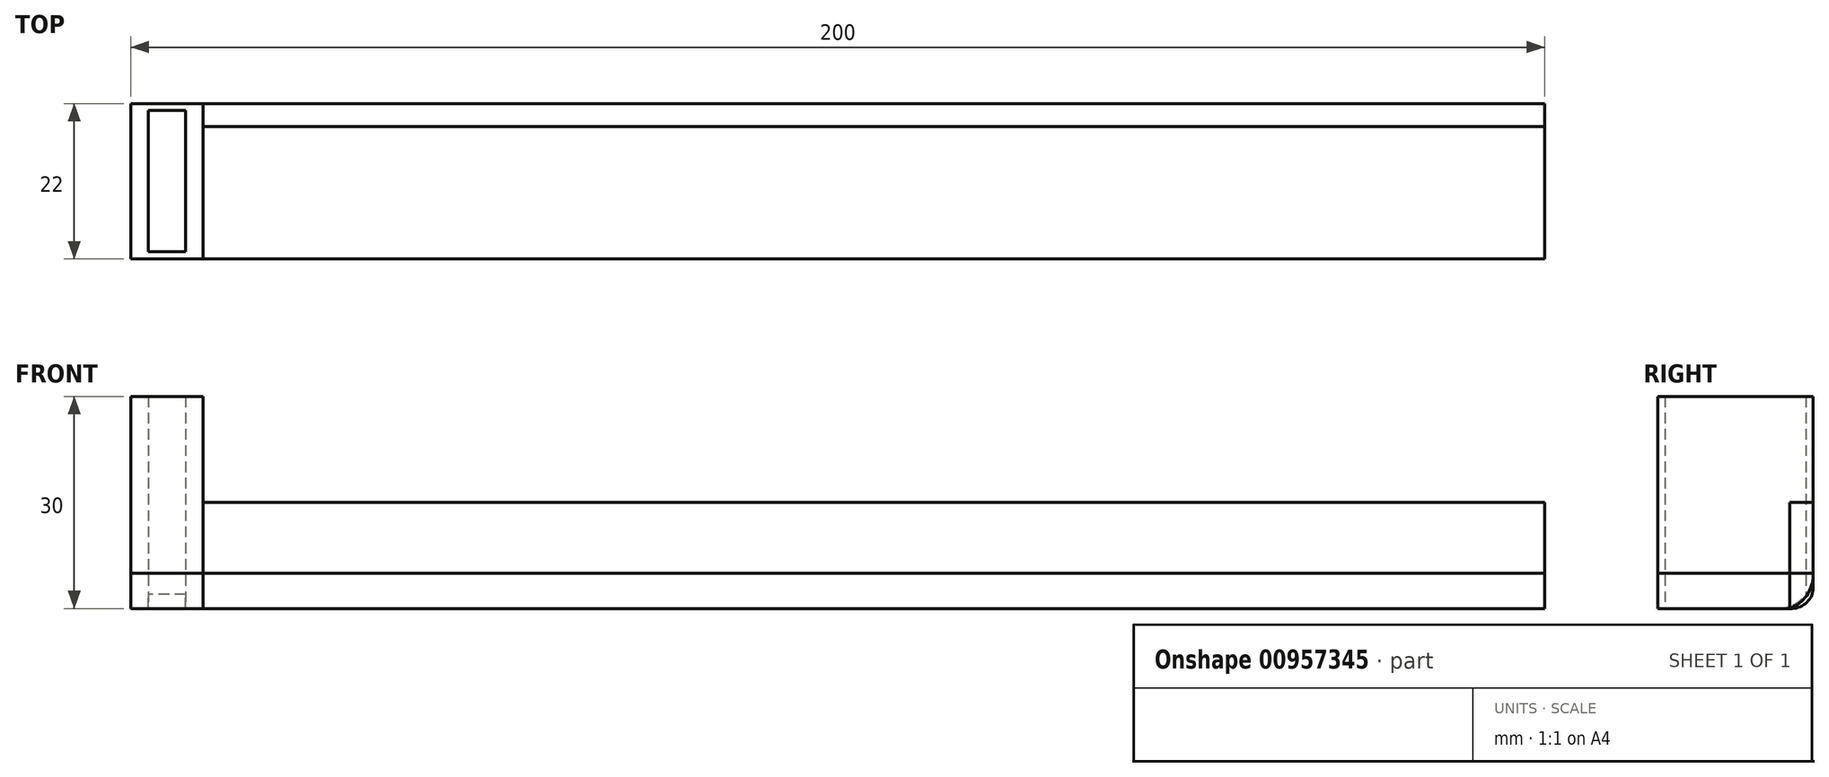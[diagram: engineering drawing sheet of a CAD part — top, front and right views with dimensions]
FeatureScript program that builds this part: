
annotation { "Feature Type Name" : "Feature", "Feature Type Description" : "" }
export const myFeature = defineFeature(function(context is Context, id is Id, definition is map)
    precondition{}
    {
        {
            var Q0;
            Q0=qCreatedBy(makeId("Top.planeOp"),FACE);
            var sketch = newSketch(context, id + "F0", { "sketchPlane" : qUnion([Q0])});
            skLineSegment(sketch, "E0.bottom", {"start": v(-42.3, 31.22) * mm, "end": v(157.7, 31.22) * mm});
            skLineSegment(sketch, "E0.top", {"start": v(-42.3, 9.22) * mm, "end": v(157.7, 9.22) * mm});
            skLineSegment(sketch, "E0.right", {"start": v(157.7, 31.22) * mm, "end": v(157.7, 9.22) * mm});
            skLineSegment(sketch, "E1", {"start": v(-32.08, 31.22) * mm, "end": v(-32.08, 9.22) * mm});
            skLineSegment(sketch, "E2", {"start": v(-42.3, 27.92) * mm, "end": v(157.7, 27.92) * mm});
            skLineSegment(sketch, "E3", {"start": v(-42.3, 31.22) * mm, "end": v(-42.3, 9.22) * mm});
            skLineSegment(sketch, "E4", {"start": v(-42.3, 30.22) * mm, "end": v(-32.08, 30.22) * mm});
            skLineSegment(sketch, "E5", {"start": v(-42.3, 20.22) * mm, "end": v(-32.08, 20.22) * mm, "construction": true});
            skLineSegment(sketch, "E6.MirrorCS", {"start": v(-42.3, 10.22) * mm, "end": v(-32.08, 10.22) * mm});
            skLineSegment(sketch, "E7", {"start": v(-39.8, 30.22) * mm, "end": v(-39.8, 10.22) * mm});
            skLineSegment(sketch, "E8", {"start": v(-34.58, 30.22) * mm, "end": v(-34.58, 10.22) * mm});
            skLineSegment(sketch, "E9", {"start": v(-39.8, 10.22) * mm, "end": v(-34.58, 10.22) * mm});
            skSolve(sketch);
        }
        {
            var Q0;
            {var subQ0=sQuery(id+"F0.wireOp",EDGE,"E7");var subQ1=sQuery(id+"F0.wireOp",EDGE,"E2");var subQ2=makeQuery(id+"F0.imprint","INTERSECT",VERTEX,{"derivedFrom":[subQ1,subQ0]});Q0=makeQuery(id+"F0.imprint","IMPRINT",FACE,{"disambiguationData":[TD([[makeQuery(id+"F0.imprint","IMPRINT",EDGE,{"disambiguationData":[TD([[subQ2,-1.0]])],"derivedFrom":subQ1}),-1.0]])]});}
            var Q1;
            {var subQ0=sQuery(id+"F0.wireOp",EDGE,"E1");var subQ1=sQuery(id+"F0.wireOp",EDGE,"E0.top");var subQ2=makeQuery(id+"F0.imprint","INTERSECT",VERTEX,{"derivedFrom":[subQ1,subQ0]});Q1=makeQuery(id+"F0.imprint","IMPRINT",FACE,{"disambiguationData":[TD([[makeQuery(id+"F0.imprint","IMPRINT",EDGE,{"disambiguationData":[TD([[subQ2,-1.0]])],"derivedFrom":subQ1}),1.0]])]});}
            var Q2;
            {var subQ0=sQuery(id+"F0.wireOp",EDGE,"E7");var subQ1=sQuery(id+"F0.wireOp",EDGE,"E2");var subQ2=makeQuery(id+"F0.imprint","INTERSECT",VERTEX,{"derivedFrom":[subQ1,subQ0]});Q2=makeQuery(id+"F0.imprint","IMPRINT",FACE,{"disambiguationData":[TD([[makeQuery(id+"F0.imprint","IMPRINT",EDGE,{"disambiguationData":[TD([[subQ2,-1.0]])],"derivedFrom":subQ1}),1.0]])]});}
            var Q3;
            {var subQ4=sQuery(id+"F0.wireOp",EDGE,"E0.top");var subQ7=sQuery(id+"F0.wireOp",EDGE,"E1");var subQ8=makeQuery(id+"F0.imprint","INTERSECT",VERTEX,{"derivedFrom":[subQ4,subQ7]});Q3=makeQuery(id+"F0.imprint","IMPRINT",FACE,{"disambiguationData":[TD([[makeQuery(id+"F0.imprint","IMPRINT",EDGE,{"disambiguationData":[TD([[subQ8,1.0]])],"derivedFrom":subQ4}),1.0]])]});}
            var Q4;
            {var subQ0=sQuery(id+"F0.wireOp",EDGE,"E2");var subQ1=sQuery(id+"F0.wireOp",EDGE,"E1");var subQ2=makeQuery(id+"F0.imprint","INTERSECT",VERTEX,{"derivedFrom":[subQ1,subQ0]});Q4=makeQuery(id+"F0.imprint","IMPRINT",FACE,{"disambiguationData":[TD([[makeQuery(id+"F0.imprint","IMPRINT",EDGE,{"disambiguationData":[TD([[subQ2,-1.0]])],"derivedFrom":subQ1}),-1.0]])]});}
            var Q5;
            {var subQ0=sQuery(id+"F0.wireOp",EDGE,"E3");var subQ1=sQuery(id+"F0.wireOp",EDGE,"E2");var subQ2=makeQuery(id+"F0.imprint","INTERSECT",VERTEX,{"derivedFrom":[subQ1,subQ0]});Q5=makeQuery(id+"F0.imprint","IMPRINT",FACE,{"disambiguationData":[TD([[makeQuery(id+"F0.imprint","IMPRINT",EDGE,{"disambiguationData":[TD([[subQ2,-1.0]])],"derivedFrom":subQ1}),-1.0]])]});}
            var Q6;
            {var subQ0=sQuery(id+"F0.wireOp",EDGE,"E3");var subQ1=sQuery(id+"F0.wireOp",EDGE,"E2");var subQ2=makeQuery(id+"F0.imprint","INTERSECT",VERTEX,{"derivedFrom":[subQ1,subQ0]});Q6=makeQuery(id+"F0.imprint","IMPRINT",FACE,{"disambiguationData":[TD([[makeQuery(id+"F0.imprint","IMPRINT",EDGE,{"disambiguationData":[TD([[subQ2,-1.0]])],"derivedFrom":subQ1}),1.0]])]});}
            var Q7;
            {var subQ5=sQuery(id+"F0.wireOp",EDGE,"E0.bottom");var subQ7=sQuery(id+"F0.wireOp",EDGE,"E1");var subQ8=makeQuery(id+"F0.imprint","INTERSECT",VERTEX,{"derivedFrom":[subQ5,subQ7]});Q7=makeQuery(id+"F0.imprint","IMPRINT",FACE,{"disambiguationData":[TD([[makeQuery(id+"F0.imprint","IMPRINT",EDGE,{"disambiguationData":[TD([[subQ8,1.0]])],"derivedFrom":subQ5}),-1.0]])]});}
            var Q8;
            {var subQ0=sQuery(id+"F0.wireOp",EDGE,"E2");var subQ1=sQuery(id+"F0.wireOp",EDGE,"E1");var subQ2=makeQuery(id+"F0.imprint","INTERSECT",VERTEX,{"derivedFrom":[subQ1,subQ0]});Q8=makeQuery(id+"F0.imprint","IMPRINT",FACE,{"disambiguationData":[TD([[makeQuery(id+"F0.imprint","IMPRINT",EDGE,{"disambiguationData":[TD([[subQ2,1.0]])],"derivedFrom":subQ1}),-1.0]])]});}
            var Q9;
            {var subQ0=sQuery(id+"F0.wireOp",EDGE,"E1");var subQ1=sQuery(id+"F0.wireOp",EDGE,"E0.bottom");var subQ2=makeQuery(id+"F0.imprint","INTERSECT",VERTEX,{"derivedFrom":[subQ1,subQ0]});Q9=makeQuery(id+"F0.imprint","IMPRINT",FACE,{"disambiguationData":[TD([[makeQuery(id+"F0.imprint","IMPRINT",EDGE,{"disambiguationData":[TD([[subQ2,-1.0]])],"derivedFrom":subQ1}),-1.0]])]});}
            extrude(context, id + "F1", {"entities" : qUnion([Q0, Q1, Q2, Q3, Q4, Q5, Q6, Q7, Q8, Q9]), "depth" : 5 * mm, "offsetDistance" : 25 * mm});
        }
        {
            var Q0;
            {var subQ5=sQuery(id+"F0.wireOp",EDGE,"E0.bottom");var subQ7=sQuery(id+"F0.wireOp",EDGE,"E1");var subQ8=makeQuery(id+"F0.imprint","INTERSECT",VERTEX,{"derivedFrom":[subQ5,subQ7]});Q0=makeQuery(id+"F0.imprint","IMPRINT",FACE,{"disambiguationData":[TD([[makeQuery(id+"F0.imprint","IMPRINT",EDGE,{"disambiguationData":[TD([[subQ8,1.0]])],"derivedFrom":subQ5}),-1.0]])]});}
            var Q1;
            {var subQ0=sQuery(id+"F0.wireOp",EDGE,"E2");var subQ1=sQuery(id+"F0.wireOp",EDGE,"E1");var subQ2=makeQuery(id+"F0.imprint","INTERSECT",VERTEX,{"derivedFrom":[subQ1,subQ0]});Q1=makeQuery(id+"F0.imprint","IMPRINT",FACE,{"disambiguationData":[TD([[makeQuery(id+"F0.imprint","IMPRINT",EDGE,{"disambiguationData":[TD([[subQ2,1.0]])],"derivedFrom":subQ1}),-1.0]])]});}
            var Q2;
            {var subQ0=sQuery(id+"F0.wireOp",EDGE,"E2");var subQ1=sQuery(id+"F0.wireOp",EDGE,"E1");var subQ2=makeQuery(id+"F0.imprint","INTERSECT",VERTEX,{"derivedFrom":[subQ1,subQ0]});Q2=makeQuery(id+"F0.imprint","IMPRINT",FACE,{"disambiguationData":[TD([[makeQuery(id+"F0.imprint","IMPRINT",EDGE,{"disambiguationData":[TD([[subQ2,-1.0]])],"derivedFrom":subQ1}),-1.0]])]});}
            var Q3;
            {var subQ0=sQuery(id+"F0.wireOp",EDGE,"E3");var subQ1=sQuery(id+"F0.wireOp",EDGE,"E2");var subQ2=makeQuery(id+"F0.imprint","INTERSECT",VERTEX,{"derivedFrom":[subQ1,subQ0]});Q3=makeQuery(id+"F0.imprint","IMPRINT",FACE,{"disambiguationData":[TD([[makeQuery(id+"F0.imprint","IMPRINT",EDGE,{"disambiguationData":[TD([[subQ2,-1.0]])],"derivedFrom":subQ1}),1.0]])]});}
            var Q4;
            {var subQ0=sQuery(id+"F0.wireOp",EDGE,"E3");var subQ1=sQuery(id+"F0.wireOp",EDGE,"E2");var subQ2=makeQuery(id+"F0.imprint","INTERSECT",VERTEX,{"derivedFrom":[subQ1,subQ0]});Q4=makeQuery(id+"F0.imprint","IMPRINT",FACE,{"disambiguationData":[TD([[makeQuery(id+"F0.imprint","IMPRINT",EDGE,{"disambiguationData":[TD([[subQ2,-1.0]])],"derivedFrom":subQ1}),-1.0]])]});}
            var Q5;
            {var subQ4=sQuery(id+"F0.wireOp",EDGE,"E0.top");var subQ7=sQuery(id+"F0.wireOp",EDGE,"E1");var subQ8=makeQuery(id+"F0.imprint","INTERSECT",VERTEX,{"derivedFrom":[subQ4,subQ7]});Q5=makeQuery(id+"F0.imprint","IMPRINT",FACE,{"disambiguationData":[TD([[makeQuery(id+"F0.imprint","IMPRINT",EDGE,{"disambiguationData":[TD([[subQ8,1.0]])],"derivedFrom":subQ4}),1.0]])]});}
            extrude(context, id + "F2", {"entities" : qUnion([Q0, Q1, Q2, Q3, Q4, Q5]), "depth" : 30 * mm, "offsetDistance" : 25 * mm});
        }
        {
            var Q0;
            {var subQ0=sQuery(id+"F0.wireOp",EDGE,"E1");var subQ1=sQuery(id+"F0.wireOp",EDGE,"E0.bottom");var subQ2=makeQuery(id+"F0.imprint","INTERSECT",VERTEX,{"derivedFrom":[subQ1,subQ0]});Q0=makeQuery(id+"F0.imprint","IMPRINT",FACE,{"disambiguationData":[TD([[makeQuery(id+"F0.imprint","IMPRINT",EDGE,{"disambiguationData":[TD([[subQ2,-1.0]])],"derivedFrom":subQ1}),-1.0]])]});}
            extrude(context, id + "F3", {"entities" : qUnion([Q0]), "depth" : 15 * mm, "offsetDistance" : 25 * mm});
        }
        {
            var Q0;
            Q0=makeQuery(id+"F2.opExtrude","CAP_EDGE",EDGE,{"disambiguationData":[OSD([sQuery(id+"F0.wireOp",EDGE,"E0.bottom")])],"isStart":true});
            var Q1;
            Q1=makeQuery(id+"F3.opExtrude","CAP_EDGE",EDGE,{"disambiguationData":[OSD([sQuery(id+"F0.wireOp",EDGE,"E0.bottom")])],"isStart":true});
            fillet(context, id + "F4", {"entities" : qUnion([Q0, Q1]), "radius" : 5 * mm, "tangentPropagation" : true, "allowEdgeOverflow" : false});
        }
        {
            var Q0;
            Q0=makeQuery(id+"F1.opExtrude","CAP_EDGE",EDGE,{"disambiguationData":[OSD([sQuery(id+"F0.wireOp",EDGE,"E0.bottom")])],"isStart":true});
            fillet(context, id + "F5", {"entities" : qUnion([Q0]), "radius" : 3 * mm, "tangentPropagation" : true, "allowEdgeOverflow" : false});
        }
    });
